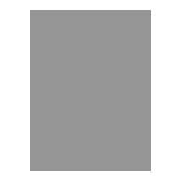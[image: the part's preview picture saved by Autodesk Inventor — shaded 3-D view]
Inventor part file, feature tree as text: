
AUTODESK INVENTOR PART (.ipt)
format: ipt  version: 2019.4 (Build 234330000, 330)  size: 115,200 bytes
history: native  units: mm (DEFAULTED — no unit token found)
features: other x4, plane x3, split x2, sketch x2
ambient origin geometry x8: Origin, YZ Plane, XZ Plane, XY Plane, X Axis, Y Axis, Z Axis, Center Point
bodies: Solid1 (feature_tree), Body (feature_tree)
feature tree (11):
  parser-record x1  (decoder bookkeeping rows leaked as tree rows — omitted from the tree; the rows remain in map.json)
  other  "Driven Length"
  other  "Start plane"
  other  "End plane"
  plane  "Work Plane5"
  split  "Split2"
  plane  "Work Plane6"
  split  "Split3"
  sketch  "Sketch3"  dims[d0=12.7mm]
  plane  "Work Plane3"
  sketch  "Sketch4"  dims[d1=12.7mm d2=112.141126mm d3=0.0mm d4=6.35mm d5=6.35mm d6=3.229026mm d7=115.370152mm d8=90.0deg d9=112.141126mm]
